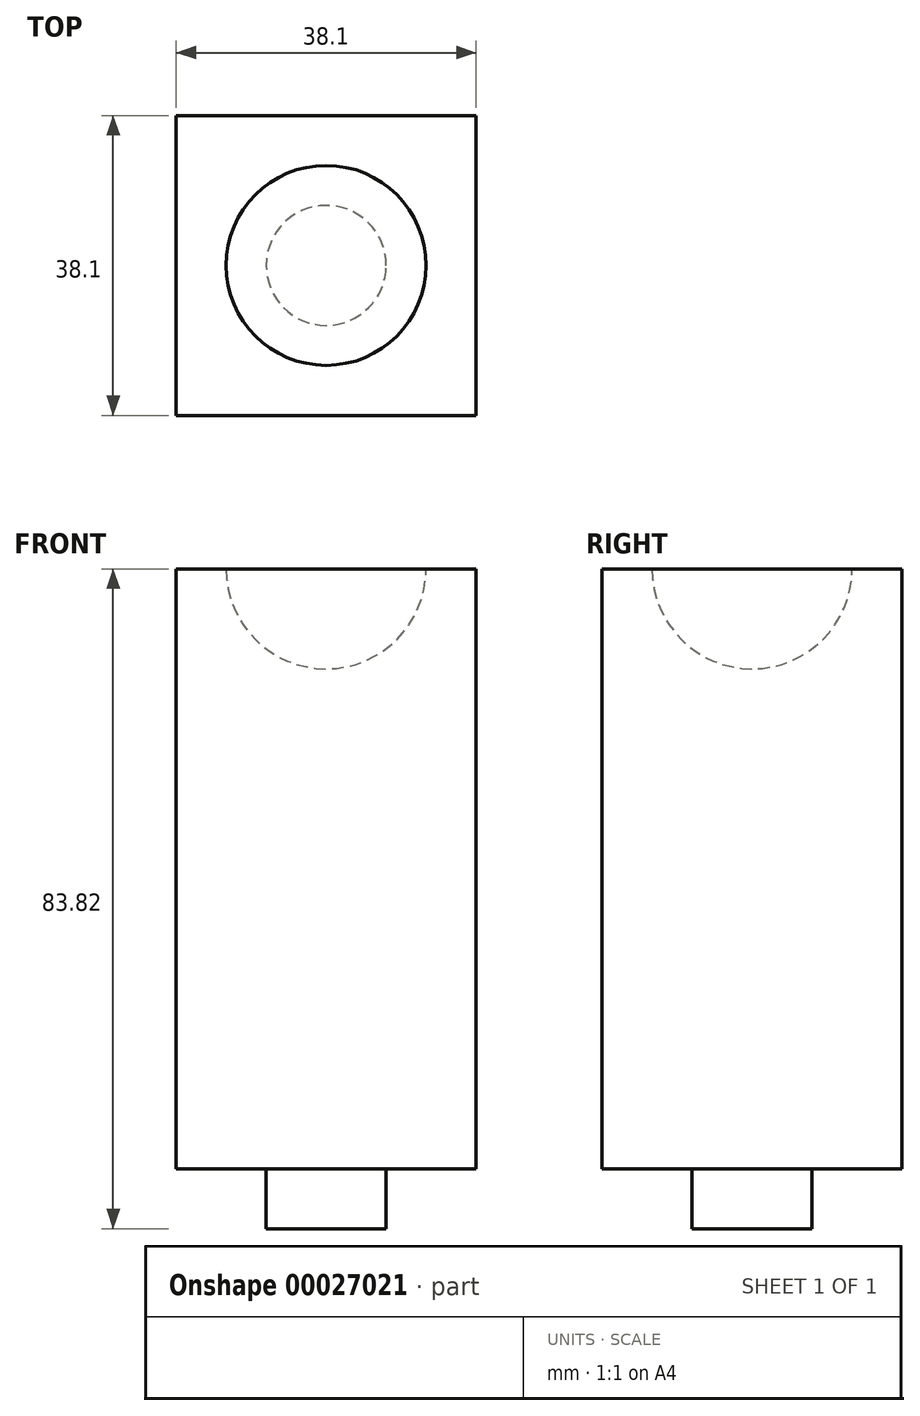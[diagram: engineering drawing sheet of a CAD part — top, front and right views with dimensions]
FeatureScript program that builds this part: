
annotation { "Feature Type Name" : "Feature", "Feature Type Description" : "" }
export const myFeature = defineFeature(function(context is Context, id is Id, definition is map)
    precondition{}
    {
        {
            var Q0;
            Q0=qCreatedBy(makeId("Front.planeOp"),FACE);
            var sketch = newSketch(context, id + "F0", { "sketchPlane" : qUnion([Q0])});
            skLineSegment(sketch, "E0.bottom", {"start": v(-29.04, 21.26) * mm, "end": v(9.06, 21.26) * mm});
            skLineSegment(sketch, "E0.top", {"start": v(-29.04, -54.94) * mm, "end": v(9.06, -54.94) * mm});
            skLineSegment(sketch, "E0.left", {"start": v(-29.04, 21.26) * mm, "end": v(-29.04, -54.94) * mm});
            skLineSegment(sketch, "E0.right", {"start": v(9.06, 21.26) * mm, "end": v(9.06, -54.94) * mm});
            skSolve(sketch);
        }
        {
            var Q0;
            Q0=makeQuery(id+"F0.imprint","IMPRINT",FACE,{"disambiguationData":[TD([[makeQuery(id+"F0.imprint","IMPRINT",EDGE,{"derivedFrom":sQuery(id+"F0.wireOp",EDGE,"E0.bottom")}),-1.0]])]});
            extrude(context, id + "F1", {"entities" : qUnion([Q0]), "depth" : 38.1 * mm});
        }
        {
            var Q0;
            Q0=makeQuery(id+"F1.opExtrude","SWEPT_FACE",FACE,{"disambiguationData":[OSD([sQuery(id+"F0.wireOp",EDGE,"E0.bottom")])]});
            var sketch = newSketch(context, id + "F2", { "sketchPlane" : qUnion([Q0])});
            skPoint(sketch, "E1", {"position": v(-10, -19.05) * mm});
            skLineSegment(sketch, "E2", {"start": v(-10, -19.05) * mm, "end": v(-22.7, -19.05) * mm});
            skLineSegment(sketch, "E3", {"start": v(-10, -19.05) * mm, "end": v(2.7, -19.05) * mm});
            skArc(sketch, "E4", {"start": v(-22.7, -19.05) * mm, "mid": v(-10, -31.75) * mm, "end": v(2.7, -19.05) * mm});
            skSolve(sketch);
        }
        {
            var Q0;
            Q0=makeQuery(id+"F2.imprint","IMPRINT",FACE,{"disambiguationData":[TD([[makeQuery(id+"F2.imprint","IMPRINT",EDGE,{"derivedFrom":sQuery(id+"F2.wireOp",EDGE,"E2")}),1.0]])]});
            var Q1;
            Q1=sQuery(id+"F2.wireOp",EDGE,"E2");
            revolve(context, id + "F3", {"operationType" : NewBodyOperationType.REMOVE, "entities" : qUnion([Q0]), "axis" : qUnion([Q1]), "revolveType" : RevolveType.FULL, "oppositeDirection" : true});
        }
        {
            var Q0;
            Q0=makeQuery(id+"F1.opExtrude","SWEPT_FACE",FACE,{"disambiguationData":[OSD([sQuery(id+"F0.wireOp",EDGE,"E0.top")])]});
            var sketch = newSketch(context, id + "F4", { "sketchPlane" : qUnion([Q0])});
            skPoint(sketch, "E5", {"position": v(-10, 19.05) * mm});
            skCircle(sketch, "E6", {"center": v(-10, 19.05) * mm, "radius": 7.62 * mm});
            skSolve(sketch);
        }
        {
            var Q0;
            Q0=makeQuery(id+"F4.imprint","IMPRINT",FACE,{"disambiguationData":[TD([[makeQuery(id+"F4.imprint","IMPRINT",EDGE,{"derivedFrom":sQuery(id+"F4.wireOp",EDGE,"E6")}),1.0]])]});
            extrude(context, id + "F5", {"entities" : qUnion([Q0]), "operationType" : NewBodyOperationType.ADD, "depth" : 7.62 * mm});
        }
    });
